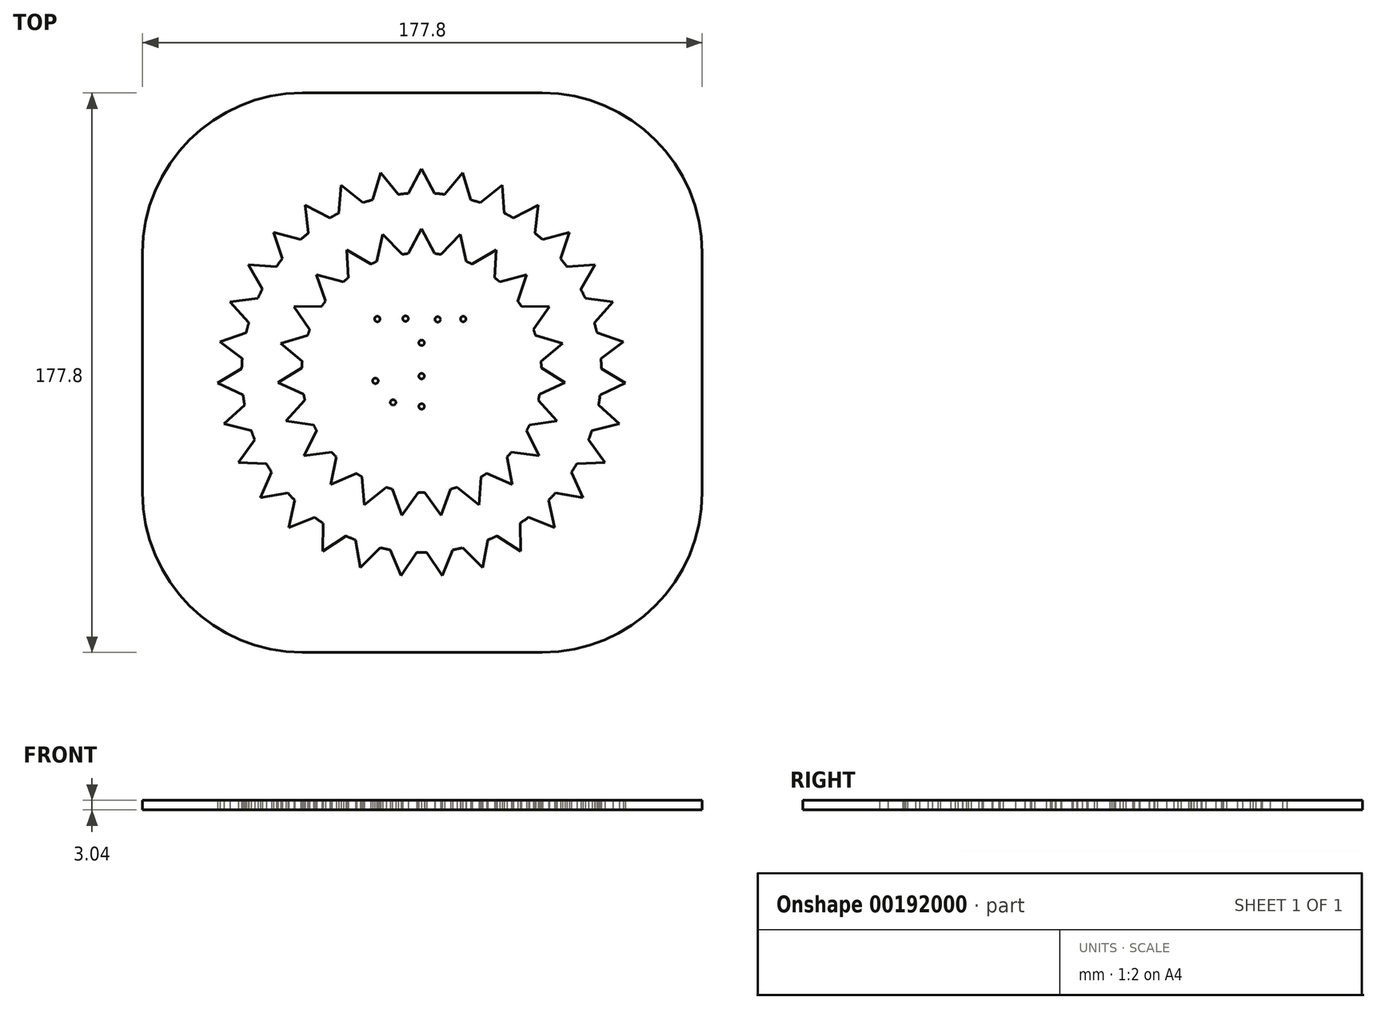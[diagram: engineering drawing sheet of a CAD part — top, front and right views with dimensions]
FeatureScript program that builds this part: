
annotation { "Feature Type Name" : "Feature", "Feature Type Description" : "" }
export const myFeature = defineFeature(function(context is Context, id is Id, definition is map)
    precondition{}
    {
        {
            var Q0;
            Q0=qCreatedBy(makeId("Top.planeOp"),FACE);
            var sketch = newSketch(context, id + "F0", { "sketchPlane" : qUnion([Q0])});
            skCircle(sketch, "E0", {"center": v(0, 0) * mm, "radius": 76.2 * mm});
            skCircle(sketch, "E1", {"center": v(0, 0) * mm, "radius": 57.15 * mm});
            skCircle(sketch, "E2", {"center": v(0, 0) * mm, "radius": 38.1 * mm});
            skCircle(sketch, "E3", {"center": v(-9.06, -9.43) * mm, "radius": 0.88 * mm});
            skCircle(sketch, "E4", {"center": v(5.12, 16.95) * mm, "radius": 0.88 * mm});
            skCircle(sketch, "E5", {"center": v(0, -1.08) * mm, "radius": 0.88 * mm});
            skCircle(sketch, "E6", {"center": v(0, -10.72) * mm, "radius": 0.88 * mm});
            skCircle(sketch, "E7", {"center": v(13.22, 17.08) * mm, "radius": 0.88 * mm});
            skCircle(sketch, "E8", {"center": v(-14.67, -2.58) * mm, "radius": 0.88 * mm});
            skCircle(sketch, "E9", {"center": v(-14.08, 17.08) * mm, "radius": 0.88 * mm});
            skCircle(sketch, "E10", {"center": v(0, 9.51) * mm, "radius": 0.88 * mm});
            skCircle(sketch, "E11", {"center": v(-5.1, 17.2) * mm, "radius": 0.88 * mm});
            skLineSegment(sketch, "E12.bottom", {"start": v(-88.65, 88.9) * mm, "end": v(89.15, 88.9) * mm});
            skLineSegment(sketch, "E12.top", {"start": v(-88.65, -88.9) * mm, "end": v(89.15, -88.9) * mm});
            skLineSegment(sketch, "E12.left", {"start": v(-88.65, 88.9) * mm, "end": v(-88.65, -88.9) * mm});
            skLineSegment(sketch, "E12.right", {"start": v(89.15, 88.9) * mm, "end": v(89.15, -88.9) * mm});
            skLineSegment(sketch, "E13", {"start": v(-4.18, 57) * mm, "end": v(0, 64.84) * mm});
            skLineSegment(sketch, "E14", {"start": v(0, 64.84) * mm, "end": v(4.18, 57) * mm});
            skLineSegment(sketch, "E15.1.0", {"start": v(-13.05, 63.52) * mm, "end": v(-7.38, 56.67) * mm});
            skLineSegment(sketch, "E15.1.1", {"start": v(-15.57, 54.99) * mm, "end": v(-13.05, 63.52) * mm});
            skLineSegment(sketch, "E15.2.0", {"start": v(-25.57, 59.59) * mm, "end": v(-18.64, 54.03) * mm});
            skLineSegment(sketch, "E15.2.1", {"start": v(-26.32, 50.73) * mm, "end": v(-25.57, 59.59) * mm});
            skLineSegment(sketch, "E16", {"start": v(-4.18, 37.87) * mm, "end": v(0, 45.72) * mm});
            skLineSegment(sketch, "E17", {"start": v(0, 45.72) * mm, "end": v(4.18, 37.87) * mm});
            skLineSegment(sketch, "E18.1.0", {"start": v(-12.33, 44.02) * mm, "end": v(-6.2, 37.6) * mm});
            skLineSegment(sketch, "E18.1.1", {"start": v(-14.24, 35.34) * mm, "end": v(-12.33, 44.02) * mm});
            skLineSegment(sketch, "E18.2.0", {"start": v(-23.75, 39.06) * mm, "end": v(-16.1, 34.53) * mm});
            skLineSegment(sketch, "E18.2.1", {"start": v(-23.25, 30.19) * mm, "end": v(-23.75, 39.06) * mm});
            skLineSegment(sketch, "E19.2.3.0", {"start": v(-37.04, 53.22) * mm, "end": v(-29.13, 49.17) * mm});
            skLineSegment(sketch, "E19.3.3.0", {"start": v(-35.99, 44.4) * mm, "end": v(-37.04, 53.22) * mm});
            skLineSegment(sketch, "E19.2.4.0", {"start": v(-47, 44.68) * mm, "end": v(-38.43, 42.3) * mm});
            skLineSegment(sketch, "E19.3.4.0", {"start": v(-44.19, 36.24) * mm, "end": v(-47, 44.68) * mm});
            skLineSegment(sketch, "E19.2.5.0", {"start": v(-55.03, 34.3) * mm, "end": v(-46.16, 33.7) * mm});
            skLineSegment(sketch, "E19.3.5.0", {"start": v(-50.58, 26.6) * mm, "end": v(-55.03, 34.3) * mm});
            skLineSegment(sketch, "E19.2.6.0", {"start": v(-60.8, 22.52) * mm, "end": v(-52, 23.71) * mm});
            skLineSegment(sketch, "E19.3.6.0", {"start": v(-54.9, 15.88) * mm, "end": v(-60.8, 22.52) * mm});
            skLineSegment(sketch, "E19.2.7.0", {"start": v(-64.1, 9.82) * mm, "end": v(-55.7, 12.76) * mm});
            skLineSegment(sketch, "E19.3.7.0", {"start": v(-56.97, 4.5) * mm, "end": v(-64.1, 9.82) * mm});
            skLineSegment(sketch, "E19.2.8.0", {"start": v(-64.76, -3.28) * mm, "end": v(-57.14, 1.29) * mm});
            skLineSegment(sketch, "E19.3.8.0", {"start": v(-56.71, -7.06) * mm, "end": v(-64.76, -3.28) * mm});
            skLineSegment(sketch, "E19.2.9.0", {"start": v(-62.77, -16.25) * mm, "end": v(-56.22, -10.24) * mm});
            skLineSegment(sketch, "E19.3.9.0", {"start": v(-54.13, -18.33) * mm, "end": v(-62.77, -16.25) * mm});
            skLineSegment(sketch, "E19.2.10.0", {"start": v(-58.22, -28.56) * mm, "end": v(-53.01, -21.35) * mm});
            skLineSegment(sketch, "E19.3.10.0", {"start": v(-49.33, -28.85) * mm, "end": v(-58.22, -28.56) * mm});
            skLineSegment(sketch, "E19.2.11.0", {"start": v(-51.28, -39.7) * mm, "end": v(-47.63, -31.58) * mm});
            skLineSegment(sketch, "E19.3.11.0", {"start": v(-42.51, -38.2) * mm, "end": v(-51.28, -39.7) * mm});
            skLineSegment(sketch, "E19.2.12.0", {"start": v(-42.24, -49.2) * mm, "end": v(-40.3, -40.53) * mm});
            skLineSegment(sketch, "E19.3.12.0", {"start": v(-33.96, -45.97) * mm, "end": v(-42.24, -49.2) * mm});
            skLineSegment(sketch, "E19.2.13.0", {"start": v(-31.47, -56.7) * mm, "end": v(-31.31, -47.8) * mm});
            skLineSegment(sketch, "E19.3.13.0", {"start": v(-24, -51.86) * mm, "end": v(-31.47, -56.7) * mm});
            skLineSegment(sketch, "E19.2.14.0", {"start": v(-19.41, -61.87) * mm, "end": v(-21.05, -53.13) * mm});
            skLineSegment(sketch, "E19.3.14.0", {"start": v(-13.08, -55.63) * mm, "end": v(-19.41, -61.87) * mm});
            skLineSegment(sketch, "E19.2.15.0", {"start": v(-6.56, -64.51) * mm, "end": v(-9.92, -56.28) * mm});
            skLineSegment(sketch, "E19.3.15.0", {"start": v(-1.6, -57.13) * mm, "end": v(-6.56, -64.51) * mm});
            skLineSegment(sketch, "E19.2.16.0", {"start": v(6.56, -64.51) * mm, "end": v(1.6, -57.13) * mm});
            skLineSegment(sketch, "E19.3.16.0", {"start": v(9.92, -56.28) * mm, "end": v(6.56, -64.51) * mm});
            skLineSegment(sketch, "E19.2.17.0", {"start": v(19.41, -61.87) * mm, "end": v(13.08, -55.63) * mm});
            skLineSegment(sketch, "E19.3.17.0", {"start": v(21.05, -53.13) * mm, "end": v(19.41, -61.87) * mm});
            skLineSegment(sketch, "E19.2.18.0", {"start": v(31.47, -56.7) * mm, "end": v(24, -51.86) * mm});
            skLineSegment(sketch, "E19.3.18.0", {"start": v(31.31, -47.8) * mm, "end": v(31.47, -56.7) * mm});
            skLineSegment(sketch, "E19.2.19.0", {"start": v(42.24, -49.2) * mm, "end": v(33.96, -45.97) * mm});
            skLineSegment(sketch, "E19.3.19.0", {"start": v(40.3, -40.53) * mm, "end": v(42.24, -49.2) * mm});
            skLineSegment(sketch, "E20.2.3.0", {"start": v(-33.41, 31.2) * mm, "end": v(-24.82, 28.9) * mm});
            skLineSegment(sketch, "E20.3.3.0", {"start": v(-30.53, 22.8) * mm, "end": v(-33.41, 31.2) * mm});
            skLineSegment(sketch, "E20.2.4.0", {"start": v(-40.6, 21.03) * mm, "end": v(-31.7, 21.13) * mm});
            skLineSegment(sketch, "E20.3.4.0", {"start": v(-35.55, 13.71) * mm, "end": v(-40.6, 21.03) * mm});
            skLineSegment(sketch, "E20.2.5.0", {"start": v(-44.76, 9.3) * mm, "end": v(-36.23, 11.8) * mm});
            skLineSegment(sketch, "E20.3.5.0", {"start": v(-37.93, 3.61) * mm, "end": v(-44.76, 9.3) * mm});
            skLineSegment(sketch, "E20.2.6.0", {"start": v(-45.61, -3.12) * mm, "end": v(-38.07, 1.58) * mm});
            skLineSegment(sketch, "E20.3.6.0", {"start": v(-37.5, -6.75) * mm, "end": v(-45.61, -3.12) * mm});
            skLineSegment(sketch, "E20.2.7.0", {"start": v(-43.08, -15.3) * mm, "end": v(-37.08, -8.74) * mm});
            skLineSegment(sketch, "E20.3.7.0", {"start": v(-34.28, -16.62) * mm, "end": v(-43.08, -15.3) * mm});
            skLineSegment(sketch, "E20.2.8.0", {"start": v(-37.35, -26.36) * mm, "end": v(-33.35, -18.43) * mm});
            skLineSegment(sketch, "E20.3.8.0", {"start": v(-28.53, -25.25) * mm, "end": v(-37.35, -26.36) * mm});
            skLineSegment(sketch, "E20.2.9.0", {"start": v(-28.85, -35.46) * mm, "end": v(-27.14, -26.74) * mm});
            skLineSegment(sketch, "E20.3.9.0", {"start": v(-20.66, -32.01) * mm, "end": v(-28.85, -35.46) * mm});
            skLineSegment(sketch, "E20.2.10.0", {"start": v(-18.21, -41.93) * mm, "end": v(-18.92, -33.07) * mm});
            skLineSegment(sketch, "E20.3.10.0", {"start": v(-11.26, -36.4) * mm, "end": v(-18.21, -41.93) * mm});
            skLineSegment(sketch, "E21.2.11.0", {"start": v(-6.23, -45.3) * mm, "end": v(-9.3, -36.95) * mm});
            skLineSegment(sketch, "E21.3.11.0", {"start": v(-1.02, -38.09) * mm, "end": v(-6.23, -45.3) * mm});
            skLineSegment(sketch, "E21.2.12.0", {"start": v(6.23, -45.3) * mm, "end": v(1.02, -38.09) * mm});
            skLineSegment(sketch, "E21.3.12.0", {"start": v(9.3, -36.95) * mm, "end": v(6.23, -45.3) * mm});
            skLineSegment(sketch, "E21.2.13.0", {"start": v(18.21, -41.93) * mm, "end": v(11.26, -36.4) * mm});
            skLineSegment(sketch, "E21.3.13.0", {"start": v(18.92, -33.07) * mm, "end": v(18.21, -41.93) * mm});
            skLineSegment(sketch, "E22.2.20.0", {"start": v(51.28, -39.7) * mm, "end": v(42.51, -38.2) * mm});
            skLineSegment(sketch, "E22.3.20.0", {"start": v(47.63, -31.58) * mm, "end": v(51.28, -39.7) * mm});
            skLineSegment(sketch, "E22.2.21.0", {"start": v(58.22, -28.56) * mm, "end": v(49.33, -28.85) * mm});
            skLineSegment(sketch, "E22.3.21.0", {"start": v(53.01, -21.35) * mm, "end": v(58.22, -28.56) * mm});
            skLineSegment(sketch, "E22.2.22.0", {"start": v(62.77, -16.25) * mm, "end": v(54.13, -18.33) * mm});
            skLineSegment(sketch, "E22.3.22.0", {"start": v(56.22, -10.24) * mm, "end": v(62.77, -16.25) * mm});
            skLineSegment(sketch, "E22.2.23.0", {"start": v(64.76, -3.28) * mm, "end": v(56.71, -7.06) * mm});
            skLineSegment(sketch, "E22.3.23.0", {"start": v(57.14, 1.29) * mm, "end": v(64.76, -3.28) * mm});
            skLineSegment(sketch, "E22.2.24.0", {"start": v(64.1, 9.82) * mm, "end": v(56.97, 4.5) * mm});
            skLineSegment(sketch, "E22.3.24.0", {"start": v(55.7, 12.76) * mm, "end": v(64.1, 9.82) * mm});
            skLineSegment(sketch, "E22.2.25.0", {"start": v(60.8, 22.52) * mm, "end": v(54.9, 15.88) * mm});
            skLineSegment(sketch, "E22.3.25.0", {"start": v(52, 23.71) * mm, "end": v(60.8, 22.52) * mm});
            skLineSegment(sketch, "E22.2.26.0", {"start": v(55.03, 34.3) * mm, "end": v(50.58, 26.6) * mm});
            skLineSegment(sketch, "E22.3.26.0", {"start": v(46.16, 33.7) * mm, "end": v(55.03, 34.3) * mm});
            skLineSegment(sketch, "E22.2.27.0", {"start": v(47, 44.68) * mm, "end": v(44.19, 36.24) * mm});
            skLineSegment(sketch, "E22.3.27.0", {"start": v(38.43, 42.3) * mm, "end": v(47, 44.68) * mm});
            skLineSegment(sketch, "E22.2.28.0", {"start": v(37.04, 53.22) * mm, "end": v(35.99, 44.4) * mm});
            skLineSegment(sketch, "E22.3.28.0", {"start": v(29.13, 49.17) * mm, "end": v(37.04, 53.22) * mm});
            skLineSegment(sketch, "E23.2.14.0", {"start": v(28.85, -35.46) * mm, "end": v(20.66, -32.01) * mm});
            skLineSegment(sketch, "E23.3.14.0", {"start": v(27.14, -26.74) * mm, "end": v(28.85, -35.46) * mm});
            skLineSegment(sketch, "E23.2.15.0", {"start": v(37.35, -26.36) * mm, "end": v(28.53, -25.25) * mm});
            skLineSegment(sketch, "E23.3.15.0", {"start": v(33.35, -18.43) * mm, "end": v(37.35, -26.36) * mm});
            skLineSegment(sketch, "E23.2.16.0", {"start": v(43.08, -15.3) * mm, "end": v(34.28, -16.62) * mm});
            skLineSegment(sketch, "E23.3.16.0", {"start": v(37.08, -8.74) * mm, "end": v(43.08, -15.3) * mm});
            skLineSegment(sketch, "E23.2.17.0", {"start": v(45.61, -3.12) * mm, "end": v(37.5, -6.75) * mm});
            skLineSegment(sketch, "E23.3.17.0", {"start": v(38.07, 1.58) * mm, "end": v(45.61, -3.12) * mm});
            skLineSegment(sketch, "E24.2.18.0", {"start": v(44.76, 9.3) * mm, "end": v(37.93, 3.61) * mm});
            skLineSegment(sketch, "E24.3.18.0", {"start": v(36.23, 11.8) * mm, "end": v(44.76, 9.3) * mm});
            skLineSegment(sketch, "E25.2.29.0", {"start": v(25.57, 59.59) * mm, "end": v(26.32, 50.73) * mm});
            skLineSegment(sketch, "E25.3.29.0", {"start": v(18.64, 54.03) * mm, "end": v(25.57, 59.59) * mm});
            skLineSegment(sketch, "E26.2.19.0", {"start": v(40.6, 21.03) * mm, "end": v(35.55, 13.71) * mm});
            skLineSegment(sketch, "E26.3.19.0", {"start": v(31.7, 21.13) * mm, "end": v(40.6, 21.03) * mm});
            skLineSegment(sketch, "E26.2.20.0", {"start": v(33.41, 31.2) * mm, "end": v(30.53, 22.8) * mm});
            skLineSegment(sketch, "E26.3.20.0", {"start": v(24.82, 28.9) * mm, "end": v(33.41, 31.2) * mm});
            skLineSegment(sketch, "E27.2.30.0", {"start": v(13.05, 63.52) * mm, "end": v(15.57, 54.99) * mm});
            skLineSegment(sketch, "E27.3.30.0", {"start": v(7.38, 56.67) * mm, "end": v(13.05, 63.52) * mm});
            skLineSegment(sketch, "E28.2.21.0", {"start": v(23.75, 39.06) * mm, "end": v(23.25, 30.19) * mm});
            skLineSegment(sketch, "E28.3.21.0", {"start": v(16.1, 34.53) * mm, "end": v(23.75, 39.06) * mm});
            skLineSegment(sketch, "E28.2.22.0", {"start": v(12.33, 44.02) * mm, "end": v(14.24, 35.34) * mm});
            skLineSegment(sketch, "E28.3.22.0", {"start": v(6.2, 37.6) * mm, "end": v(12.33, 44.02) * mm});
            skSolve(sketch);
        }
        {
            var Q0;
            Q0=makeQuery(id+"F0.imprint","IMPRINT",FACE,{"disambiguationData":[TD([[makeQuery(id+"F0.imprint","IMPRINT",EDGE,{"derivedFrom":sQuery(id+"F0.wireOp",EDGE,"E0")}),-1.0]])]});
            var Q1;
            Q1=makeQuery(id+"F0.imprint","IMPRINT",FACE,{"disambiguationData":[TD([[makeQuery(id+"F0.imprint","IMPRINT",EDGE,{"derivedFrom":sQuery(id+"F0.wireOp",EDGE,"E0")}),1.0]])]});
            var Q2;
            {var subQ0=sQuery(id+"F0.wireOp",EDGE,"E18.1.0");Q2=makeQuery(id+"F0.imprint","IMPRINT",FACE,{"disambiguationData":[TD([[makeQuery(id+"F0.imprint","IMPRINT",EDGE,{"derivedFrom":subQ0}),-1.0]])]});}
            var Q3;
            {var subQ0=sQuery(id+"F0.wireOp",EDGE,"E18.2.0");Q3=makeQuery(id+"F0.imprint","IMPRINT",FACE,{"disambiguationData":[TD([[makeQuery(id+"F0.imprint","IMPRINT",EDGE,{"derivedFrom":subQ0}),-1.0]])]});}
            var Q4;
            {var subQ0=sQuery(id+"F0.wireOp",EDGE,"E20.2.3.0");Q4=makeQuery(id+"F0.imprint","IMPRINT",FACE,{"disambiguationData":[TD([[makeQuery(id+"F0.imprint","IMPRINT",EDGE,{"derivedFrom":subQ0}),-1.0]])]});}
            var Q5;
            {var subQ0=sQuery(id+"F0.wireOp",EDGE,"E20.2.4.0");Q5=makeQuery(id+"F0.imprint","IMPRINT",FACE,{"disambiguationData":[TD([[makeQuery(id+"F0.imprint","IMPRINT",EDGE,{"derivedFrom":subQ0}),-1.0]])]});}
            var Q6;
            Q6=makeQuery(id+"F0.imprint","IMPRINT",FACE,{"disambiguationData":[TD([[makeQuery(id+"F0.imprint","IMPRINT",EDGE,{"derivedFrom":sQuery(id+"F0.wireOp",EDGE,"E3")}),-1.0]])]});
            var Q7;
            {var subQ0=sQuery(id+"F0.wireOp",EDGE,"E20.2.5.0");Q7=makeQuery(id+"F0.imprint","IMPRINT",FACE,{"disambiguationData":[TD([[makeQuery(id+"F0.imprint","IMPRINT",EDGE,{"derivedFrom":subQ0}),-1.0]])]});}
            var Q8;
            {var subQ0=sQuery(id+"F0.wireOp",EDGE,"E20.2.6.0");Q8=makeQuery(id+"F0.imprint","IMPRINT",FACE,{"disambiguationData":[TD([[makeQuery(id+"F0.imprint","IMPRINT",EDGE,{"derivedFrom":subQ0}),-1.0]])]});}
            var Q9;
            {var subQ0=sQuery(id+"F0.wireOp",EDGE,"E20.2.7.0");Q9=makeQuery(id+"F0.imprint","IMPRINT",FACE,{"disambiguationData":[TD([[makeQuery(id+"F0.imprint","IMPRINT",EDGE,{"derivedFrom":subQ0}),-1.0]])]});}
            var Q10;
            {var subQ0=sQuery(id+"F0.wireOp",EDGE,"E20.2.8.0");Q10=makeQuery(id+"F0.imprint","IMPRINT",FACE,{"disambiguationData":[TD([[makeQuery(id+"F0.imprint","IMPRINT",EDGE,{"derivedFrom":subQ0}),-1.0]])]});}
            var Q11;
            {var subQ0=sQuery(id+"F0.wireOp",EDGE,"E20.2.10.0");Q11=makeQuery(id+"F0.imprint","IMPRINT",FACE,{"disambiguationData":[TD([[makeQuery(id+"F0.imprint","IMPRINT",EDGE,{"derivedFrom":subQ0}),-1.0]])]});}
            var Q12;
            {var subQ0=sQuery(id+"F0.wireOp",EDGE,"E21.2.11.0");Q12=makeQuery(id+"F0.imprint","IMPRINT",FACE,{"disambiguationData":[TD([[makeQuery(id+"F0.imprint","IMPRINT",EDGE,{"derivedFrom":subQ0}),-1.0]])]});}
            var Q13;
            {var subQ0=sQuery(id+"F0.wireOp",EDGE,"E20.2.9.0");Q13=makeQuery(id+"F0.imprint","IMPRINT",FACE,{"disambiguationData":[TD([[makeQuery(id+"F0.imprint","IMPRINT",EDGE,{"derivedFrom":subQ0}),-1.0]])]});}
            var Q14;
            {var subQ0=sQuery(id+"F0.wireOp",EDGE,"E21.2.12.0");Q14=makeQuery(id+"F0.imprint","IMPRINT",FACE,{"disambiguationData":[TD([[makeQuery(id+"F0.imprint","IMPRINT",EDGE,{"derivedFrom":subQ0}),-1.0]])]});}
            var Q15;
            {var subQ0=sQuery(id+"F0.wireOp",EDGE,"E21.2.13.0");Q15=makeQuery(id+"F0.imprint","IMPRINT",FACE,{"disambiguationData":[TD([[makeQuery(id+"F0.imprint","IMPRINT",EDGE,{"derivedFrom":subQ0}),-1.0]])]});}
            var Q16;
            {var subQ0=sQuery(id+"F0.wireOp",EDGE,"E23.2.14.0");Q16=makeQuery(id+"F0.imprint","IMPRINT",FACE,{"disambiguationData":[TD([[makeQuery(id+"F0.imprint","IMPRINT",EDGE,{"derivedFrom":subQ0}),-1.0]])]});}
            var Q17;
            {var subQ0=sQuery(id+"F0.wireOp",EDGE,"E23.2.15.0");Q17=makeQuery(id+"F0.imprint","IMPRINT",FACE,{"disambiguationData":[TD([[makeQuery(id+"F0.imprint","IMPRINT",EDGE,{"derivedFrom":subQ0}),-1.0]])]});}
            var Q18;
            {var subQ0=sQuery(id+"F0.wireOp",EDGE,"E16");Q18=makeQuery(id+"F0.imprint","IMPRINT",FACE,{"disambiguationData":[TD([[makeQuery(id+"F0.imprint","IMPRINT",EDGE,{"derivedFrom":subQ0}),-1.0]])]});}
            var Q19;
            {var subQ0=sQuery(id+"F0.wireOp",EDGE,"E28.2.22.0");Q19=makeQuery(id+"F0.imprint","IMPRINT",FACE,{"disambiguationData":[TD([[makeQuery(id+"F0.imprint","IMPRINT",EDGE,{"derivedFrom":subQ0}),-1.0]])]});}
            var Q20;
            {var subQ0=sQuery(id+"F0.wireOp",EDGE,"E28.2.21.0");Q20=makeQuery(id+"F0.imprint","IMPRINT",FACE,{"disambiguationData":[TD([[makeQuery(id+"F0.imprint","IMPRINT",EDGE,{"derivedFrom":subQ0}),-1.0]])]});}
            var Q21;
            {var subQ0=sQuery(id+"F0.wireOp",EDGE,"E26.2.20.0");Q21=makeQuery(id+"F0.imprint","IMPRINT",FACE,{"disambiguationData":[TD([[makeQuery(id+"F0.imprint","IMPRINT",EDGE,{"derivedFrom":subQ0}),-1.0]])]});}
            var Q22;
            {var subQ0=sQuery(id+"F0.wireOp",EDGE,"E26.2.19.0");Q22=makeQuery(id+"F0.imprint","IMPRINT",FACE,{"disambiguationData":[TD([[makeQuery(id+"F0.imprint","IMPRINT",EDGE,{"derivedFrom":subQ0}),-1.0]])]});}
            var Q23;
            {var subQ0=sQuery(id+"F0.wireOp",EDGE,"E24.2.18.0");Q23=makeQuery(id+"F0.imprint","IMPRINT",FACE,{"disambiguationData":[TD([[makeQuery(id+"F0.imprint","IMPRINT",EDGE,{"derivedFrom":subQ0}),-1.0]])]});}
            var Q24;
            {var subQ0=sQuery(id+"F0.wireOp",EDGE,"E23.2.17.0");Q24=makeQuery(id+"F0.imprint","IMPRINT",FACE,{"disambiguationData":[TD([[makeQuery(id+"F0.imprint","IMPRINT",EDGE,{"derivedFrom":subQ0}),-1.0]])]});}
            var Q25;
            {var subQ0=sQuery(id+"F0.wireOp",EDGE,"E23.2.16.0");Q25=makeQuery(id+"F0.imprint","IMPRINT",FACE,{"disambiguationData":[TD([[makeQuery(id+"F0.imprint","IMPRINT",EDGE,{"derivedFrom":subQ0}),-1.0]])]});}
            extrude(context, id + "F1", {"entities" : qUnion([Q0, Q1, Q2, Q3, Q4, Q5, Q6, Q7, Q8, Q9, Q10, Q11, Q12, Q13, Q14, Q15, Q16, Q17, Q18, Q19, Q20, Q21, Q22, Q23, Q24, Q25]), "endBound" : BoundingType.SYMMETRIC, "depth" : 3.05 * mm});
        }
        {
            var Q0;
            Q0=makeQuery(id+"F1.opExtrude","SWEPT_EDGE",EDGE,{"disambiguationData":[OSD([sQuery(id+"F0.wireOp",EDGE,"E12.bottom"),sQuery(id+"F0.wireOp",EDGE,"E12.left")])]});
            var Q1;
            Q1=makeQuery(id+"F1.opExtrude","SWEPT_EDGE",EDGE,{"disambiguationData":[OSD([sQuery(id+"F0.wireOp",EDGE,"E12.top"),sQuery(id+"F0.wireOp",EDGE,"E12.left")])]});
            var Q2;
            Q2=makeQuery(id+"F1.opExtrude","SWEPT_EDGE",EDGE,{"disambiguationData":[OSD([sQuery(id+"F0.wireOp",EDGE,"E12.top"),sQuery(id+"F0.wireOp",EDGE,"E12.right")])]});
            var Q3;
            Q3=makeQuery(id+"F1.opExtrude","SWEPT_EDGE",EDGE,{"disambiguationData":[OSD([sQuery(id+"F0.wireOp",EDGE,"E12.bottom"),sQuery(id+"F0.wireOp",EDGE,"E12.right")])]});
            fillet(context, id + "F2", {"entities" : qUnion([Q0, Q1, Q2, Q3]), "radius" : 50.8 * mm, "tangentPropagation" : true, "allowEdgeOverflow" : false});
        }
    });
